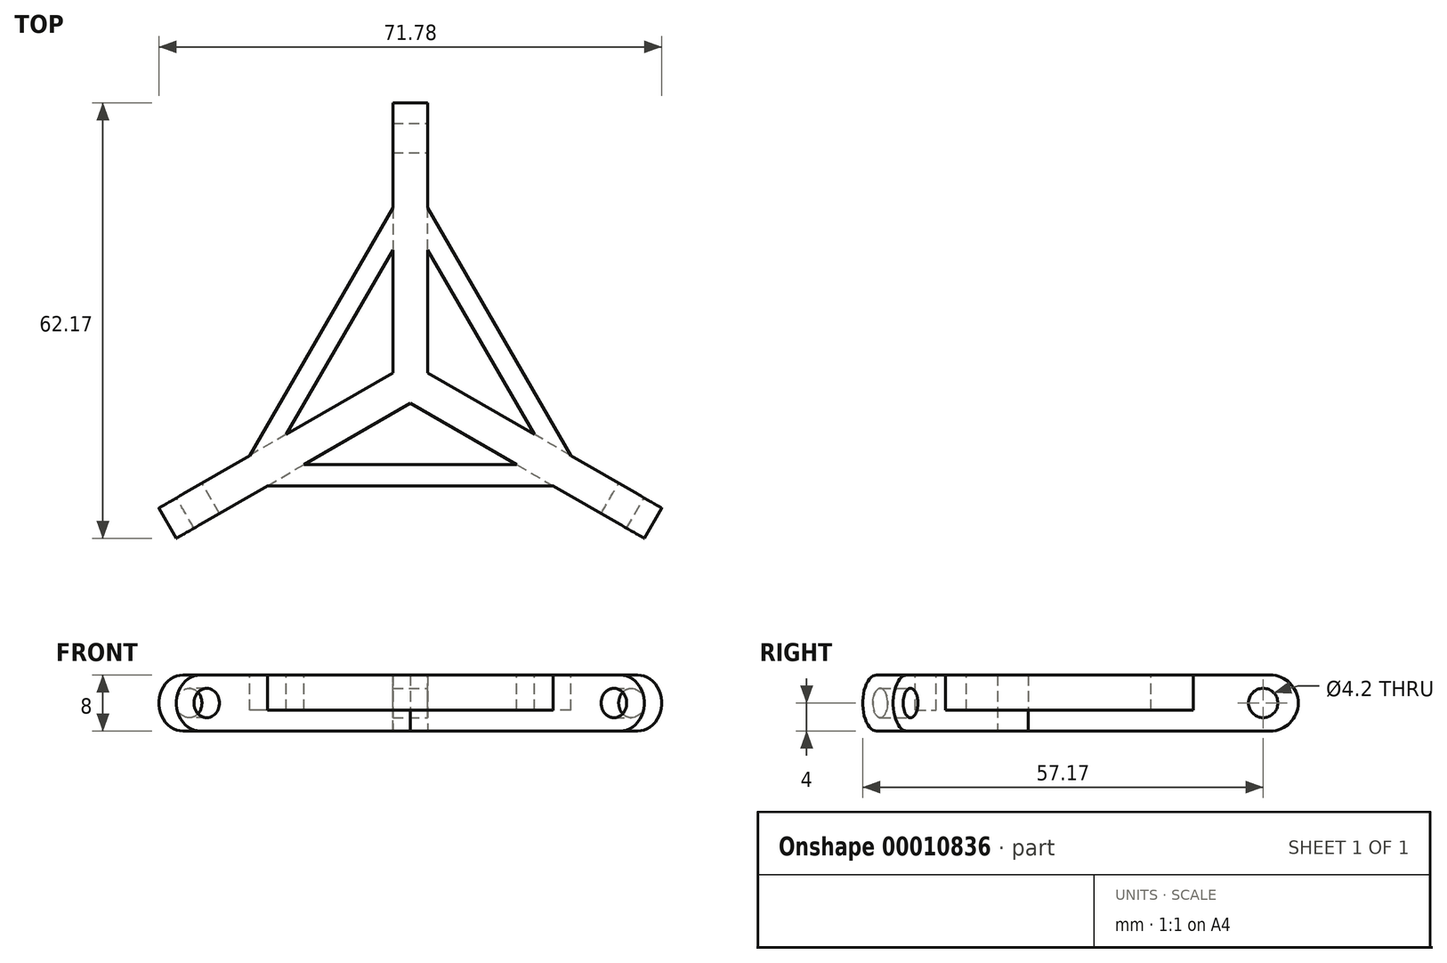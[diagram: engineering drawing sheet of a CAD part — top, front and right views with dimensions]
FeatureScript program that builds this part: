
annotation { "Feature Type Name" : "Feature", "Feature Type Description" : "" }
export const myFeature = defineFeature(function(context is Context, id is Id, definition is map)
    precondition{}
    {
        {
            var Q0;
            Q0=qCreatedBy(makeId("Top.planeOp"),FACE);
            var sketch = newSketch(context, id + "F0", { "sketchPlane" : qUnion([Q0])});
            skLineSegment(sketch, "E0", {"start": v(0, 0) * mm, "end": v(0, 42.55) * mm, "construction": true});
            skLineSegment(sketch, "E1", {"start": v(0, 0) * mm, "end": v(41.35, -23.87) * mm, "construction": true});
            skLineSegment(sketch, "E2", {"start": v(0, 0) * mm, "end": v(-33.63, -19.42) * mm, "construction": true});
            skLineSegment(sketch, "E3", {"start": v(2.5, 40) * mm, "end": v(-2.5, 40) * mm});
            skLineSegment(sketch, "E4", {"start": v(-2.5, 40) * mm, "end": v(-2.5, 1.44) * mm});
            skLineSegment(sketch, "E5", {"start": v(-2.5, 1.44) * mm, "end": v(-35.9, -17.83) * mm});
            skLineSegment(sketch, "E6", {"start": v(-35.9, -17.83) * mm, "end": v(-33.4, -22.17) * mm});
            skLineSegment(sketch, "E7", {"start": v(-33.4, -22.17) * mm, "end": v(0, -2.89) * mm});
            skLineSegment(sketch, "E8", {"start": v(0, -2.89) * mm, "end": v(33.4, -22.17) * mm});
            skLineSegment(sketch, "E9", {"start": v(33.4, -22.17) * mm, "end": v(35.9, -17.83) * mm});
            skLineSegment(sketch, "E10", {"start": v(35.9, -17.83) * mm, "end": v(2.5, 1.44) * mm});
            skLineSegment(sketch, "E11", {"start": v(2.5, 1.44) * mm, "end": v(2.5, 40) * mm});
            skSolve(sketch);
        }
        {
            var Q0;
            Q0=makeQuery(id+"F0.imprint","IMPRINT",FACE,{"disambiguationData":[TD([[makeQuery(id+"F0.imprint","IMPRINT",EDGE,{"derivedFrom":sQuery(id+"F0.wireOp",EDGE,"E3")}),1.0]])]});
            extrude(context, id + "F1", {"entities" : qUnion([Q0]), "depth" : 8 * mm});
        }
        {
            var Q0;
            Q0=makeQuery(id+"F1.opExtrude","SWEPT_FACE",FACE,{"disambiguationData":[OSD([sQuery(id+"F0.wireOp",EDGE,"E11")])]});
            var sketch = newSketch(context, id + "F2", { "sketchPlane" : qUnion([Q0])});
            skCircle(sketch, "E12", {"center": v(35, 4) * mm, "radius": 2.1 * mm});
            skPoint(sketch, "E12.centerSnap0", {"position": v(40, 4) * mm});
            skSolve(sketch);
        }
        {
            var Q0;
            Q0=makeQuery(id+"F1.opExtrude","SWEPT_FACE",FACE,{"disambiguationData":[OSD([sQuery(id+"F0.wireOp",EDGE,"E10")])]});
            var sketch = newSketch(context, id + "F3", { "sketchPlane" : qUnion([Q0])});
            skCircle(sketch, "E13", {"center": v(-35, 4) * mm, "radius": 2.1 * mm});
            skPoint(sketch, "E13.centerSnap0", {"position": v(-40, 4) * mm});
            skSolve(sketch);
        }
        {
            var Q0;
            Q0=makeQuery(id+"F1.opExtrude","SWEPT_FACE",FACE,{"disambiguationData":[OSD([sQuery(id+"F0.wireOp",EDGE,"E5")])]});
            var sketch = newSketch(context, id + "F4", { "sketchPlane" : qUnion([Q0])});
            skCircle(sketch, "E14", {"center": v(35, 4) * mm, "radius": 2.1 * mm});
            skPoint(sketch, "E14.centerSnap0", {"position": v(40, 4) * mm});
            skSolve(sketch);
        }
        {
            var Q0;
            Q0=makeQuery(id+"F4.imprint","IMPRINT",FACE,{"disambiguationData":[TD([[makeQuery(id+"F4.imprint","IMPRINT",EDGE,{"derivedFrom":sQuery(id+"F4.wireOp",EDGE,"E14")}),1.0]])]});
            extrude(context, id + "F5", {"entities" : qUnion([Q0]), "operationType" : NewBodyOperationType.REMOVE, "oppositeDirection" : true, "depth" : 25 * mm});
        }
        {
            var Q0;
            Q0=makeQuery(id+"F2.imprint","IMPRINT",FACE,{"disambiguationData":[TD([[makeQuery(id+"F2.imprint","IMPRINT",EDGE,{"derivedFrom":sQuery(id+"F2.wireOp",EDGE,"E12")}),1.0]])]});
            extrude(context, id + "F6", {"entities" : qUnion([Q0]), "operationType" : NewBodyOperationType.REMOVE, "oppositeDirection" : true, "depth" : 25 * mm});
        }
        {
            var Q0;
            Q0=makeQuery(id+"F3.imprint","IMPRINT",FACE,{"disambiguationData":[TD([[makeQuery(id+"F3.imprint","IMPRINT",EDGE,{"derivedFrom":sQuery(id+"F3.wireOp",EDGE,"E13")}),1.0]])]});
            extrude(context, id + "F7", {"entities" : qUnion([Q0]), "operationType" : NewBodyOperationType.REMOVE, "oppositeDirection" : true, "depth" : 25 * mm});
        }
        {
            var Q0;
            Q0=makeQuery(id+"F1.opExtrude","CAP_FACE",FACE,{"disambiguationData":[OSD([sQuery(id+"F0.wireOp",EDGE,"E3"),sQuery(id+"F0.wireOp",EDGE,"E4"),sQuery(id+"F0.wireOp",EDGE,"E5"),sQuery(id+"F0.wireOp",EDGE,"E6"),sQuery(id+"F0.wireOp",EDGE,"E7"),sQuery(id+"F0.wireOp",EDGE,"E8"),sQuery(id+"F0.wireOp",EDGE,"E9"),sQuery(id+"F0.wireOp",EDGE,"E10"),sQuery(id+"F0.wireOp",EDGE,"E11")])],"isStart":false});
            var sketch = newSketch(context, id + "F8", { "sketchPlane" : qUnion([Q0])});
            skLineSegment(sketch, "E15", {"start": v(-34.5, -118.57) * mm, "end": v(-34.5, 170.9) * mm, "construction": true});
            skLineSegment(sketch, "E16", {"start": v(2, 40) * mm, "end": v(-53.08, 40) * mm, "construction": true});
            skPoint(sketch, "E16.endSnap0", {"position": v(0, 40) * mm});
            skLineSegment(sketch, "E17", {"start": v(0, 0) * mm, "end": v(-34.5, 40) * mm, "construction": true});
            skLineSegment(sketch, "E18", {"start": v(0, 0) * mm, "end": v(29.28, 83.97) * mm, "construction": true});
            skLineSegment(sketch, "E19", {"start": v(0, 0) * mm, "end": v(35.97, -41.7) * mm, "construction": true});
            skLineSegment(sketch, "E20", {"start": v(0, 0) * mm, "end": v(-47.98, -9.13) * mm, "construction": true});
            skLineSegment(sketch, "E21", {"start": v(-2.5, 25) * mm, "end": v(-22.9, -10.33) * mm});
            skLineSegment(sketch, "E22", {"start": v(-17.7, -7.33) * mm, "end": v(-2.5, 19) * mm});
            skLineSegment(sketch, "E23.1.0", {"start": v(-20.4, -14.67) * mm, "end": v(20.4, -14.67) * mm});
            skLineSegment(sketch, "E23.1.1", {"start": v(15.2, -11.67) * mm, "end": v(-15.2, -11.67) * mm});
            skLineSegment(sketch, "E23.2.0", {"start": v(22.9, -10.33) * mm, "end": v(2.5, 25) * mm});
            skLineSegment(sketch, "E23.2.1", {"start": v(2.5, 19) * mm, "end": v(17.7, -7.33) * mm});
            skPoint(sketch, "E23.center", {"position": v(0, 0) * mm});
            skSolve(sketch);
        }
        {
            var Q0;
            {var subQ0=sQuery(id+"F8.wireOp",EDGE,"E21");Q0=makeQuery(id+"F8.imprint","IMPRINT",FACE,{"disambiguationData":[TD([[makeQuery(id+"F8.imprint","IMPRINT",EDGE,{"derivedFrom":subQ0}),1.0]])]});}
            var Q1;
            {var subQ0=sQuery(id+"F8.wireOp",EDGE,"E23.1.0");Q1=makeQuery(id+"F8.imprint","IMPRINT",FACE,{"disambiguationData":[TD([[makeQuery(id+"F8.imprint","IMPRINT",EDGE,{"derivedFrom":subQ0}),1.0]])]});}
            var Q2;
            {var subQ0=sQuery(id+"F8.wireOp",EDGE,"E23.2.0");Q2=makeQuery(id+"F8.imprint","IMPRINT",FACE,{"disambiguationData":[TD([[makeQuery(id+"F8.imprint","IMPRINT",EDGE,{"derivedFrom":subQ0}),1.0]])]});}
            extrude(context, id + "F9", {"entities" : qUnion([Q0, Q1, Q2]), "operationType" : NewBodyOperationType.ADD, "oppositeDirection" : true, "depth" : 5 * mm});
        }
        {
            var Q0;
            Q0=makeQuery(id+"F1.opExtrude","CAP_EDGE",EDGE,{"disambiguationData":[OSD([sQuery(id+"F0.wireOp",EDGE,"E6")])],"isStart":true});
            var Q1;
            Q1=makeQuery(id+"F1.opExtrude","CAP_EDGE",EDGE,{"disambiguationData":[OSD([sQuery(id+"F0.wireOp",EDGE,"E6")])],"isStart":false});
            var Q2;
            Q2=makeQuery(id+"F1.opExtrude","CAP_EDGE",EDGE,{"disambiguationData":[OSD([sQuery(id+"F0.wireOp",EDGE,"E3")])],"isStart":true});
            var Q3;
            Q3=makeQuery(id+"F1.opExtrude","CAP_EDGE",EDGE,{"disambiguationData":[OSD([sQuery(id+"F0.wireOp",EDGE,"E3")])],"isStart":false});
            var Q4;
            Q4=makeQuery(id+"F1.opExtrude","CAP_EDGE",EDGE,{"disambiguationData":[OSD([sQuery(id+"F0.wireOp",EDGE,"E9")])],"isStart":true});
            var Q5;
            Q5=makeQuery(id+"F1.opExtrude","CAP_EDGE",EDGE,{"disambiguationData":[OSD([sQuery(id+"F0.wireOp",EDGE,"E9")])],"isStart":false});
            fillet(context, id + "F10", {"entities" : qUnion([Q0, Q1, Q2, Q3, Q4, Q5]), "radius" : 4 * mm, "tangentPropagation" : true, "allowEdgeOverflow" : false});
        }
    });
